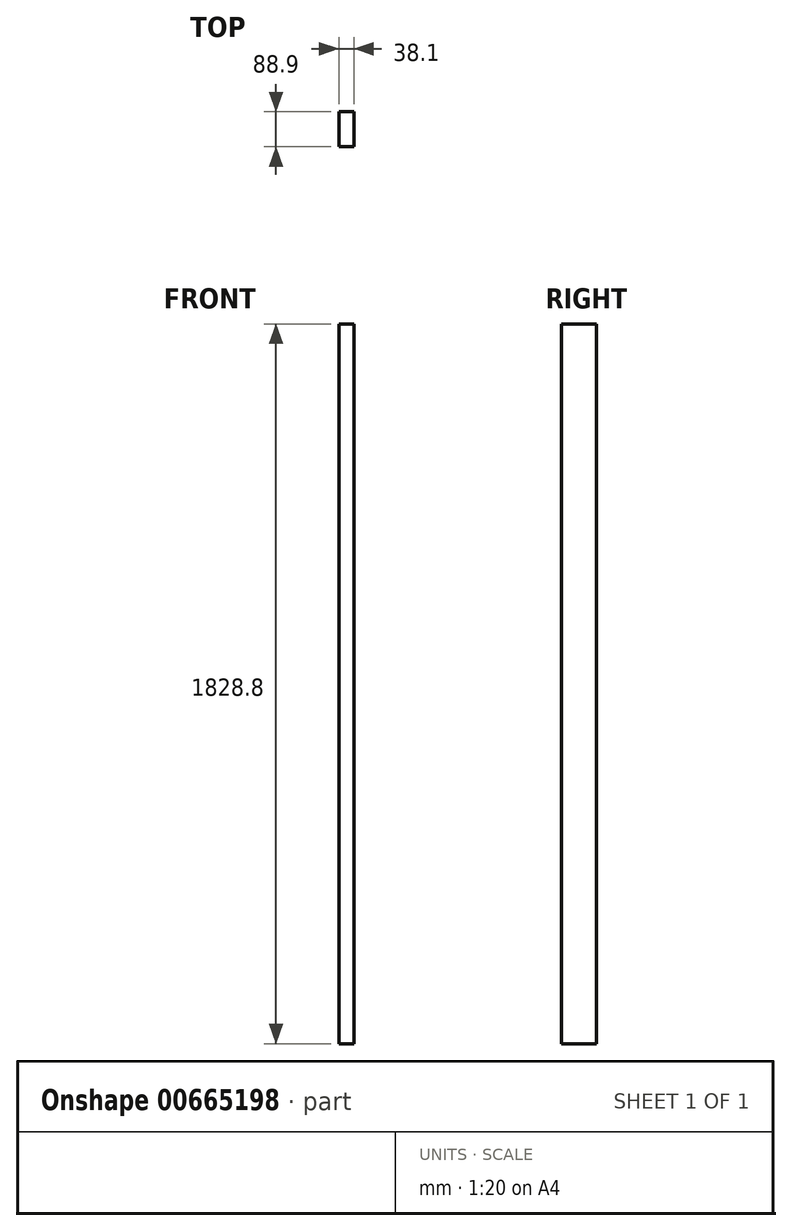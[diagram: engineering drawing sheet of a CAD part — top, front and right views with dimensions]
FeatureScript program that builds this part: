
annotation { "Feature Type Name" : "Feature", "Feature Type Description" : "" }
export const myFeature = defineFeature(function(context is Context, id is Id, definition is map)
    precondition{}
    {
        {
            var Q0;
            Q0=qCreatedBy(makeId("Top.planeOp"),FACE);
            var sketch = newSketch(context, id + "F0", { "sketchPlane" : qUnion([Q0])});
            skLineSegment(sketch, "E0.bottom", {"start": v(19.05, 44.45) * mm, "end": v(-19.05, 44.45) * mm});
            skLineSegment(sketch, "E0.top", {"start": v(19.05, -44.45) * mm, "end": v(-19.05, -44.45) * mm});
            skLineSegment(sketch, "E0.left", {"start": v(19.05, 44.45) * mm, "end": v(19.05, -44.45) * mm});
            skLineSegment(sketch, "E0.right", {"start": v(-19.05, 44.45) * mm, "end": v(-19.05, -44.45) * mm});
            skPoint(sketch, "E0.middle", {"position": v(0, 0) * mm});
            skSolve(sketch);
        }
        {
            var Q0;
            Q0=makeQuery(id+"F0.imprint","IMPRINT",FACE,{"disambiguationData":[TD([[makeQuery(id+"F0.imprint","IMPRINT",EDGE,{"derivedFrom":sQuery(id+"F0.wireOp",EDGE,"E0.bottom")}),1.0]])]});
            extrude(context, id + "F1", {"entities" : qUnion([Q0]), "depth" : 1828.8 * mm, "offsetDistance" : 25.4 * mm});
        }
    });
